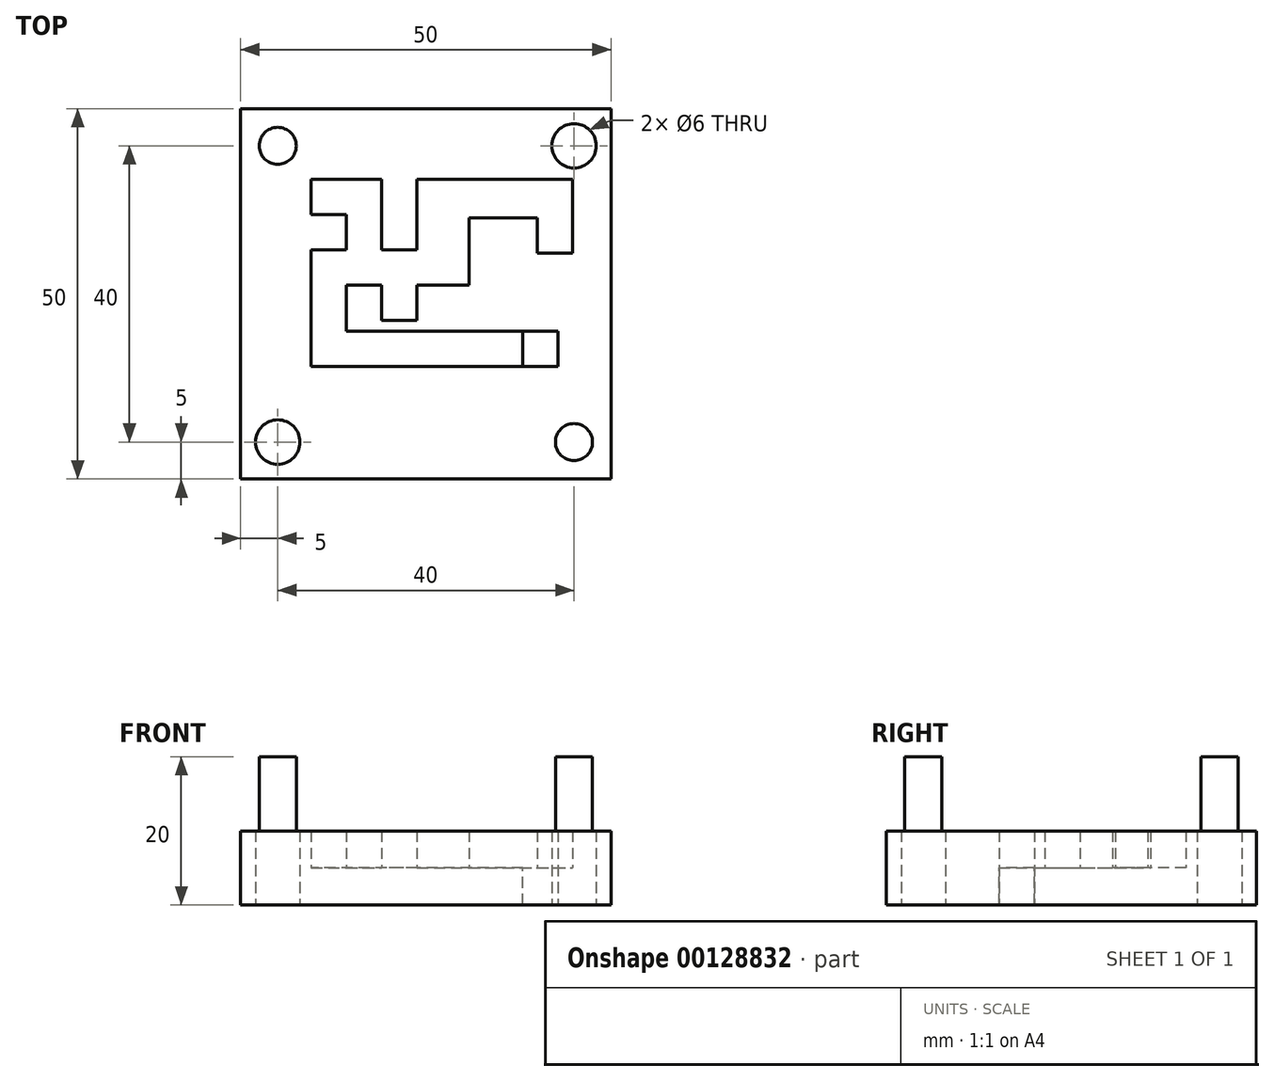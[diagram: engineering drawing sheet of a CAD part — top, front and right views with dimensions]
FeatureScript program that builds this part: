
annotation { "Feature Type Name" : "Feature", "Feature Type Description" : "" }
export const myFeature = defineFeature(function(context is Context, id is Id, definition is map)
    precondition{}
    {
        {
            var Q0;
            Q0=qCreatedBy(makeId("Top.planeOp"),FACE);
            var sketch = newSketch(context, id + "F0", { "sketchPlane" : qUnion([Q0])});
            skLineSegment(sketch, "E0.bottom", {"start": v(0, 0) * mm, "end": v(50, 0) * mm});
            skLineSegment(sketch, "E0.top", {"start": v(0, -50) * mm, "end": v(50, -50) * mm});
            skLineSegment(sketch, "E0.left", {"start": v(0, 0) * mm, "end": v(0, -50) * mm});
            skLineSegment(sketch, "E0.right", {"start": v(50, 0) * mm, "end": v(50, -50) * mm});
            skLineSegment(sketch, "E1", {"start": v(25, 0) * mm, "end": v(25, -50) * mm, "construction": true});
            skLineSegment(sketch, "E2", {"start": v(0, -25) * mm, "end": v(50, -25) * mm, "construction": true});
            skPoint(sketch, "E3", {"position": v(38.1, -34.78) * mm});
            skLineSegment(sketch, "E4.top", {"start": v(38.1, -30.02) * mm, "end": v(42.86, -30.02) * mm});
            skLineSegment(sketch, "E4.right", {"start": v(42.86, -34.78) * mm, "end": v(42.86, -30.02) * mm});
            skPoint(sketch, "E5", {"position": v(9.52, -9.53) * mm});
            skLineSegment(sketch, "E6", {"start": v(9.52, -9.53) * mm, "end": v(9.52, -14.29) * mm});
            skLineSegment(sketch, "E7", {"start": v(9.52, -9.53) * mm, "end": v(19.05, -9.53) * mm});
            skLineSegment(sketch, "E8.MirrorCS", {"start": v(28.57, -9.52) * mm, "end": v(23.81, -9.52) * mm});
            skLineSegment(sketch, "E9.MirrorCS", {"start": v(9.52, -28.57) * mm, "end": v(9.52, -19.05) * mm});
            skLineSegment(sketch, "E10.MirrorCS", {"start": v(23.81, -28.57) * mm, "end": v(19.05, -28.57) * mm});
            skLineSegment(sketch, "E11.MirrorCS", {"start": v(30.85, -14.7) * mm, "end": v(30.85, -19.46) * mm});
            skLineSegment(sketch, "E12", {"start": v(30.85, -14.7) * mm, "end": v(40.04, -14.7) * mm});
            skLineSegment(sketch, "E13", {"start": v(28.57, -9.52) * mm, "end": v(38.8, -9.52) * mm});
            skPoint(sketch, "E14.orphan", {"position": v(30.85, -9.94) * mm});
            skLineSegment(sketch, "E15", {"start": v(38.1, -30.02) * mm, "end": v(38.1, -34.78) * mm});
            skPoint(sketch, "E16.orphan", {"position": v(9.52, -28.57) * mm});
            skLineSegment(sketch, "E17", {"start": v(23.81, -9.52) * mm, "end": v(23.81, -19.05) * mm});
            skLineSegment(sketch, "E18", {"start": v(23.81, -28.57) * mm, "end": v(23.81, -23.81) * mm});
            skLineSegment(sketch, "E19", {"start": v(19.05, -9.53) * mm, "end": v(19.05, -19.05) * mm});
            skLineSegment(sketch, "E20", {"start": v(23.81, -19.05) * mm, "end": v(19.05, -19.05) * mm});
            skPoint(sketch, "E21.orphan", {"position": v(19.05, -9.53) * mm});
            skLineSegment(sketch, "E22", {"start": v(14.29, -23.81) * mm, "end": v(19.05, -23.81) * mm});
            skLineSegment(sketch, "E23", {"start": v(19.05, -28.57) * mm, "end": v(19.05, -23.81) * mm});
            skLineSegment(sketch, "E24", {"start": v(14.29, -28.57) * mm, "end": v(14.29, -23.81) * mm});
            skPoint(sketch, "E25.orphan", {"position": v(9.52, -23.81) * mm});
            skLineSegment(sketch, "E26", {"start": v(9.52, -14.29) * mm, "end": v(14.29, -14.29) * mm});
            skLineSegment(sketch, "E27", {"start": v(9.52, -19.05) * mm, "end": v(14.29, -19.05) * mm});
            skLineSegment(sketch, "E28", {"start": v(14.29, -19.05) * mm, "end": v(14.29, -14.29) * mm});
            skLineSegment(sketch, "E29", {"start": v(38.8, -9.52) * mm, "end": v(44.8, -9.52) * mm});
            skLineSegment(sketch, "E30", {"start": v(44.8, -9.52) * mm, "end": v(44.8, -19.46) * mm});
            skLineSegment(sketch, "E31", {"start": v(40.04, -14.7) * mm, "end": v(40.04, -19.46) * mm});
            skLineSegment(sketch, "E32", {"start": v(40.04, -19.46) * mm, "end": v(44.8, -19.46) * mm});
            skLineSegment(sketch, "E33", {"start": v(38.1, -34.78) * mm, "end": v(42.86, -34.78) * mm});
            skLineSegment(sketch, "E34", {"start": v(30.85, -23.81) * mm, "end": v(30.85, -19.46) * mm});
            skLineSegment(sketch, "E35", {"start": v(23.81, -23.81) * mm, "end": v(30.85, -23.81) * mm});
            skCircle(sketch, "E36", {"center": v(45, -5) * mm, "radius": 3 * mm});
            skCircle(sketch, "E37", {"center": v(5, -45) * mm, "radius": 3 * mm});
            skLineSegment(sketch, "E38", {"start": v(38.1, -30.02) * mm, "end": v(14.29, -30.02) * mm});
            skLineSegment(sketch, "E39", {"start": v(14.29, -30.02) * mm, "end": v(14.29, -28.57) * mm});
            skLineSegment(sketch, "E40", {"start": v(38.1, -34.78) * mm, "end": v(9.52, -34.78) * mm});
            skLineSegment(sketch, "E41", {"start": v(9.52, -34.78) * mm, "end": v(9.52, -28.57) * mm});
            skSolve(sketch);
        }
        {
            var Q0;
            Q0=makeQuery(id+"F0.imprint","IMPRINT",FACE,{"disambiguationData":[TD([[makeQuery(id+"F0.imprint","IMPRINT",EDGE,{"derivedFrom":sQuery(id+"F0.wireOp",EDGE,"E0.bottom")}),-1.0]])]});
            extrude(context, id + "F1", {"entities" : qUnion([Q0]), "endBound" : BoundingType.SYMMETRIC, "depth" : 10 * mm});
        }
        {
            var Q0;
            Q0=makeQuery(id+"F0.imprint","IMPRINT",FACE,{"disambiguationData":[TD([[makeQuery(id+"F0.imprint","IMPRINT",EDGE,{"derivedFrom":sQuery(id+"F0.wireOp",EDGE,"E6")}),1.0]])]});
            extrude(context, id + "F2", {"entities" : qUnion([Q0]), "operationType" : NewBodyOperationType.ADD, "oppositeDirection" : true, "depth" : 5 * mm});
        }
        {
            var Q0;
            Q0=makeQuery(id+"F1.opExtrude","CAP_FACE",FACE,{"disambiguationData":[OSD([sQuery(id+"F0.wireOp",EDGE,"E0.bottom"),sQuery(id+"F0.wireOp",EDGE,"E0.top"),sQuery(id+"F0.wireOp",EDGE,"E0.left"),sQuery(id+"F0.wireOp",EDGE,"E0.right"),sQuery(id+"F0.wireOp",EDGE,"E4.top"),sQuery(id+"F0.wireOp",EDGE,"E4.right"),sQuery(id+"F0.wireOp",EDGE,"E6"),sQuery(id+"F0.wireOp",EDGE,"E7"),sQuery(id+"F0.wireOp",EDGE,"E8.MirrorCS"),sQuery(id+"F0.wireOp",EDGE,"E9.MirrorCS"),sQuery(id+"F0.wireOp",EDGE,"E10.MirrorCS"),sQuery(id+"F0.wireOp",EDGE,"E11.MirrorCS"),sQuery(id+"F0.wireOp",EDGE,"E12"),sQuery(id+"F0.wireOp",EDGE,"E13"),sQuery(id+"F0.wireOp",EDGE,"E17"),sQuery(id+"F0.wireOp",EDGE,"E18"),sQuery(id+"F0.wireOp",EDGE,"E19"),sQuery(id+"F0.wireOp",EDGE,"E20"),sQuery(id+"F0.wireOp",EDGE,"E22"),sQuery(id+"F0.wireOp",EDGE,"E23"),sQuery(id+"F0.wireOp",EDGE,"E24"),sQuery(id+"F0.wireOp",EDGE,"E26"),sQuery(id+"F0.wireOp",EDGE,"E27"),sQuery(id+"F0.wireOp",EDGE,"E28"),sQuery(id+"F0.wireOp",EDGE,"E29"),sQuery(id+"F0.wireOp",EDGE,"E30"),sQuery(id+"F0.wireOp",EDGE,"E31"),sQuery(id+"F0.wireOp",EDGE,"E32"),sQuery(id+"F0.wireOp",EDGE,"E33"),sQuery(id+"F0.wireOp",EDGE,"E34"),sQuery(id+"F0.wireOp",EDGE,"E35"),sQuery(id+"F0.wireOp",EDGE,"E36"),sQuery(id+"F0.wireOp",EDGE,"E37"),sQuery(id+"F0.wireOp",EDGE,"E38"),sQuery(id+"F0.wireOp",EDGE,"E39"),sQuery(id+"F0.wireOp",EDGE,"E40"),sQuery(id+"F0.wireOp",EDGE,"E41")])],"isStart":false});
            var sketch = newSketch(context, id + "F3", { "sketchPlane" : qUnion([Q0])});
            skCircle(sketch, "E42", {"center": v(5, -5) * mm, "radius": 2.5 * mm});
            skCircle(sketch, "E43", {"center": v(45, -45) * mm, "radius": 2.5 * mm});
            skSolve(sketch);
        }
        {
            var Q0;
            Q0=makeQuery(id+"F3.imprint","IMPRINT",FACE,{"disambiguationData":[TD([[makeQuery(id+"F3.imprint","IMPRINT",EDGE,{"derivedFrom":sQuery(id+"F3.wireOp",EDGE,"E42")}),1.0]])]});
            var Q1;
            Q1=makeQuery(id+"F3.imprint","IMPRINT",FACE,{"disambiguationData":[TD([[makeQuery(id+"F3.imprint","IMPRINT",EDGE,{"derivedFrom":sQuery(id+"F3.wireOp",EDGE,"E43")}),1.0]])]});
            extrude(context, id + "F4", {"entities" : qUnion([Q0, Q1]), "operationType" : NewBodyOperationType.ADD, "depth" : 10 * mm});
        }
    });
